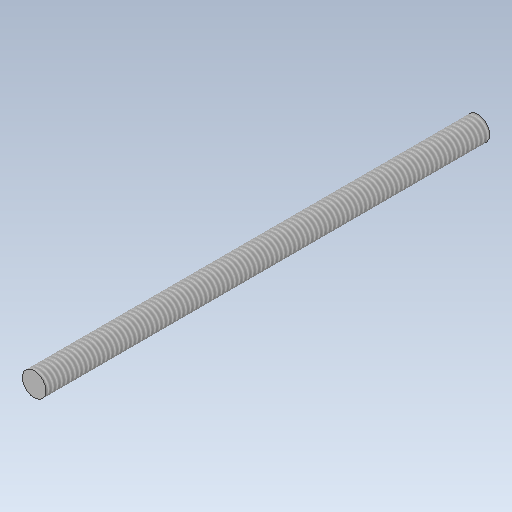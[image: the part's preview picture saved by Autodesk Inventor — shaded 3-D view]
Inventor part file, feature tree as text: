
AUTODESK INVENTOR PART (.ipt)
format: ipt  version: 2020 (Build 240168000, 168)  size: 107,008 bytes
history: native  units: mm
features: extrude x1, thread x1, sketch x1
ambient origin geometry x8: Origin, YZ Plane, XZ Plane, XY Plane, X Axis, Y Axis, Z Axis, Center Point
bodies: Solid1 (feature_tree)
feature tree (3):
  extrude  "Extrusion1"  Depth=150.0mm TaperAngle=0.0deg
  thread  "Thread1"  [1 undecoded]
  sketch  "Sketch1"  dims[d0=8.0mm d1=150.0mm d2=0.0mm d3=550.0mm d4=0.0mm]
note: 1 required parameter value undecoded (feature->parameter linkage not recoverable at this tier; creation-order binding heuristic only, values carry confidence <= 0.55)
